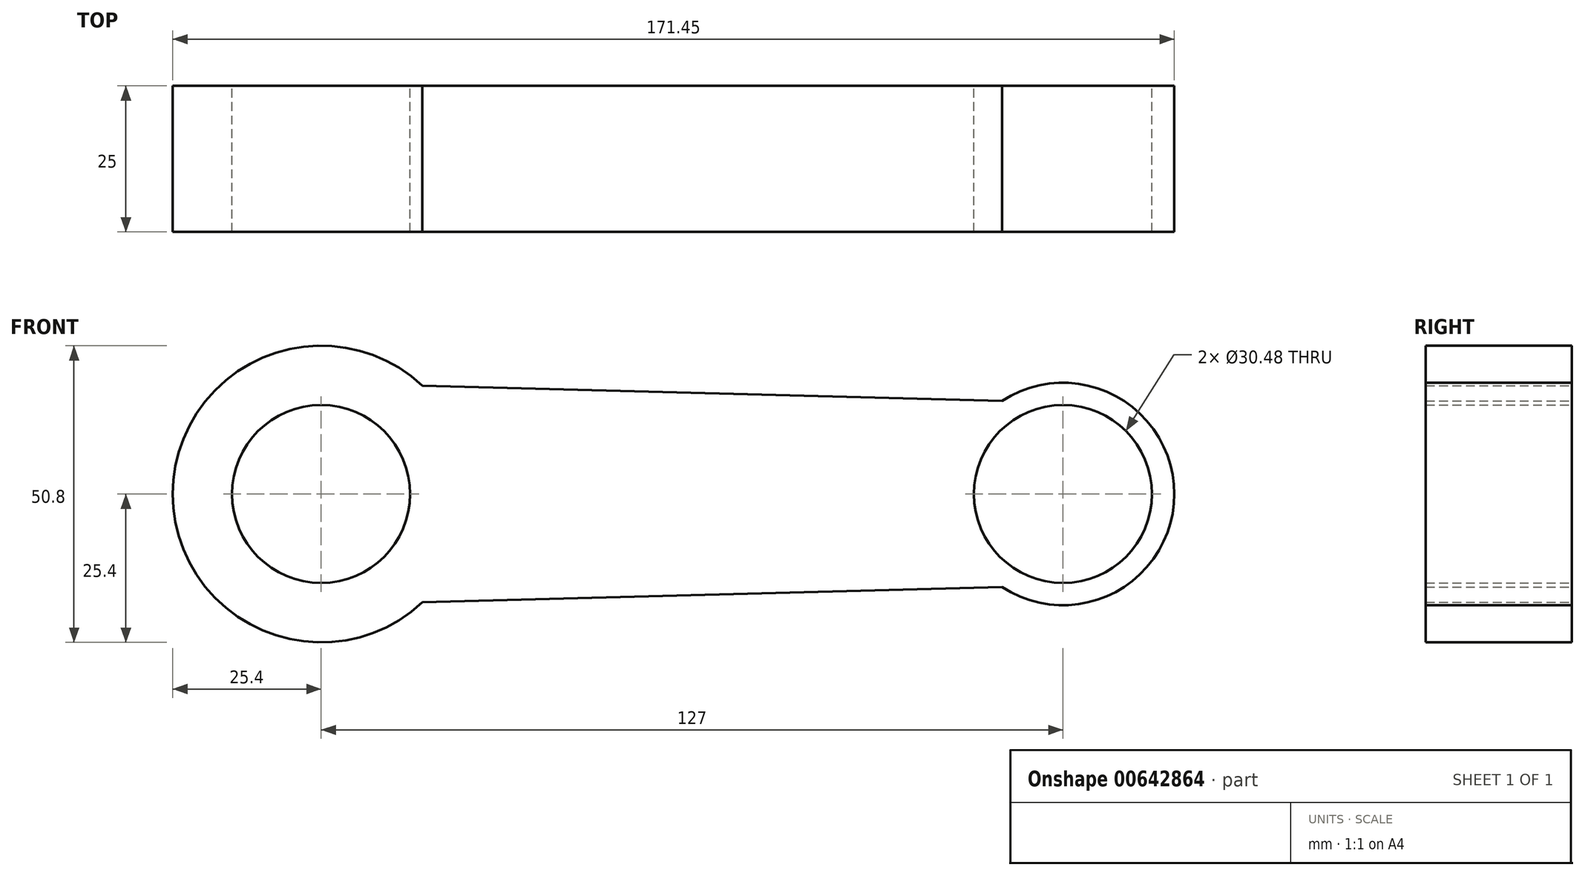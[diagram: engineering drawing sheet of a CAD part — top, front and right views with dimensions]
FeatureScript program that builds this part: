
annotation { "Feature Type Name" : "Feature", "Feature Type Description" : "" }
export const myFeature = defineFeature(function(context is Context, id is Id, definition is map)
    precondition{}
    {
        {
            var Q0;
            Q0=qCreatedBy(makeId("Front.planeOp"),FACE);
            var sketch = newSketch(context, id + "F0", { "sketchPlane" : qUnion([Q0])});
            skCircle(sketch, "E0", {"center": v(0, 0) * mm, "radius": 25.4 * mm});
            skCircle(sketch, "E1", {"center": v(127, 0) * mm, "radius": 19.05 * mm});
            skLineSegment(sketch, "E2", {"start": v(0, 0) * mm, "end": v(127, 0) * mm, "construction": true});
            skLineSegment(sketch, "E3.MirrorCS", {"start": v(17.34, 18.56) * mm, "end": v(116.6, 15.96) * mm});
            skLineSegment(sketch, "E4.MirrorCS", {"start": v(17.34, -18.56) * mm, "end": v(116.6, -15.96) * mm});
            skCircle(sketch, "E5", {"center": v(0, 0) * mm, "radius": 15.24 * mm});
            skCircle(sketch, "E6", {"center": v(127, 0) * mm, "radius": 15.24 * mm});
            skSolve(sketch);
        }
        {
            var Q0;
            {var subQ0=sQuery(id+"F0.wireOp",EDGE,"E3.MirrorCS");Q0=makeQuery(id+"F0.imprint","IMPRINT",FACE,{"disambiguationData":[TD([[makeQuery(id+"F0.imprint","IMPRINT",EDGE,{"derivedFrom":subQ0}),-1.0]])]});}
            var Q1;
            Q1=makeQuery(id+"F0.imprint","IMPRINT",FACE,{"disambiguationData":[TD([[makeQuery(id+"F0.imprint","IMPRINT",EDGE,{"derivedFrom":sQuery(id+"F0.wireOp",EDGE,"E5")}),-1.0]])]});
            var Q2;
            Q2=makeQuery(id+"F0.imprint","IMPRINT",FACE,{"disambiguationData":[TD([[makeQuery(id+"F0.imprint","IMPRINT",EDGE,{"derivedFrom":sQuery(id+"F0.wireOp",EDGE,"E6")}),-1.0]])]});
            var Q3;
            Q3 = qSketchRegion(id + "FegPXUoMCUBkc4P_1", true);
            extrude(context, id + "F1", {"entities" : qUnion([Q0, Q1, Q2, Q3]), "depth" : 25 * mm, "offsetDistance" : 25 * mm});
        }
    });
